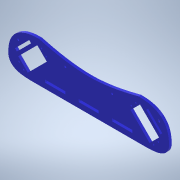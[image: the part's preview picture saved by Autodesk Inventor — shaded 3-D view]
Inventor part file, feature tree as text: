
AUTODESK INVENTOR PART (.ipt)
format: ipt  version: 2020.3 (Build 243373000, 373)  size: 258,560 bytes
history: native  units: mm
features: extrude x5, sketch x5, projected_geometry x2, move_body x2, direct_edit x1
ambient origin geometry x8: Origin, YZ Plane, XZ Plane, XY Plane, X Axis, Y Axis, Z Axis, Center Point
bodies: Solid1 (feature_tree)
feature tree (15):
  extrude  "Extrusion1"  TaperAngle=0.0deg  [1 undecoded]
  extrude  "Extrusion2"  TaperAngle=0.0deg  [1 undecoded]
  extrude  "Extrusion3"  TaperAngle=0.0deg  [1 undecoded]
  extrude  "Extrusion4"  [1 undecoded]
  extrude  "Extrusion5"  [1 undecoded]
  direct_edit  "Direct Edit1"
  sketch  "Sketch1"  dims[d2=4.0mm d3=0.0mm d8=0.0mm d9=0.0mm]
  sketch  "Sketch2"  dims[d10=0.0mm d11=0.0mm d19=0.0mm d20=0.0mm]
  sketch  "Sketch3"  dims[d23=10.0mm d24=0.0mm d25=0.0mm d26=-15.0mm d27=0.0mm]
  projected_geometry  "Projected Loop1"
  sketch  "Sketch4"  dims[d28=0.0mm d29=-15.0mm d30=0.0mm]
  sketch  "Sketch5"
  projected_geometry  "Projected Loop2"
  move_body  "Move1"
  move_body  "Move2"
note: 5 required parameter values undecoded (feature->parameter linkage not recoverable at this tier; creation-order binding heuristic only, values carry confidence <= 0.55)
